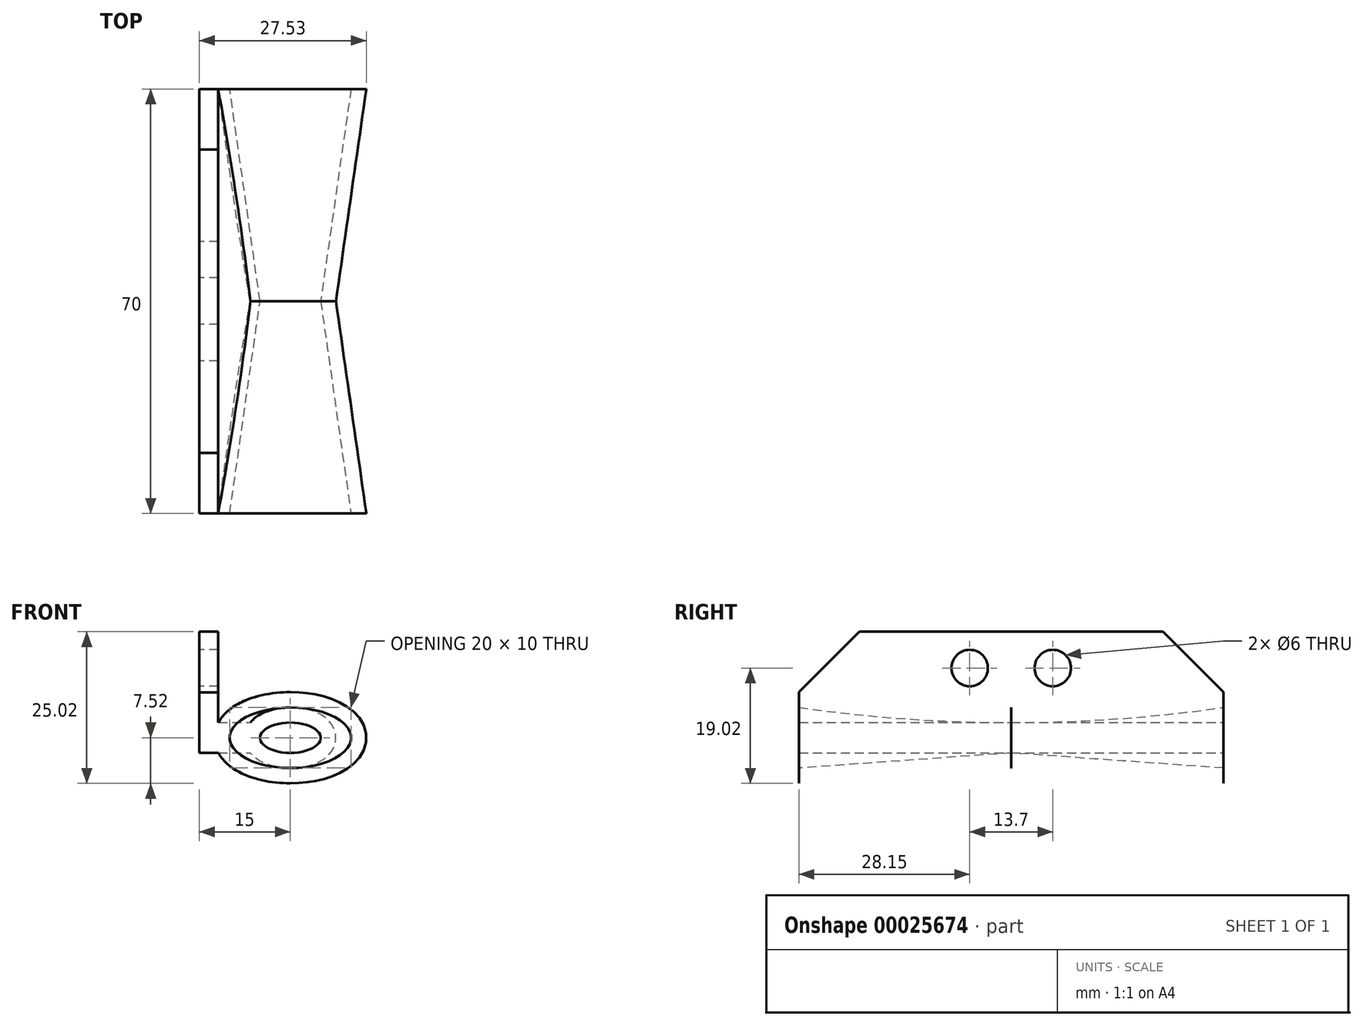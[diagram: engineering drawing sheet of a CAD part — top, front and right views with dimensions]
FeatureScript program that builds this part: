
annotation { "Feature Type Name" : "Feature", "Feature Type Description" : "" }
export const myFeature = defineFeature(function(context is Context, id is Id, definition is map)
    precondition{}
    {
        {
            var Q0;
            Q0=qCreatedBy(makeId("Front.planeOp"),FACE);
            var sketch = newSketch(context, id + "F0", { "sketchPlane" : qUnion([Q0])});
            skEllipticalArc(sketch, "E0", {});
            skLineSegment(sketch, "E1", {"start": v(0, -2.5) * mm, "end": v(0, 2.5) * mm});
            const initialGuessF0  = {"E0": [0, 0, 1, 0, 0.005, 0.0025, 4.71238898038469, 1.5707963267948966]};
            skSetInitialGuess(sketch, initialGuessF0);
            skSolve(sketch);
        }
        {
            var Q0;
            Q0=qCreatedBy(makeId("Front.planeOp"),FACE);
            cPlane(context, id + "F1", {"entities" : qUnion([Q0]), "cplaneType" : CPlaneType.OFFSET, "offset" : 35 * mm, "width" : 150 * mm, "height" : 150 * mm});
        }
        {
            var Q0;
            Q0=qCreatedBy(id+"F1.planeOp",FACE);
            var sketch = newSketch(context, id + "F2", { "sketchPlane" : qUnion([Q0])});
            skEllipticalArc(sketch, "E2", {});
            skLineSegment(sketch, "E3", {"start": v(0, -5) * mm, "end": v(0, 5) * mm});
            const initialGuessF2  = {"E2": [0, 0, 1, 0, 0.01, 0.005, 4.71238898038469, 1.5707963267948966]};
            skSetInitialGuess(sketch, initialGuessF2);
            skSolve(sketch);
        }
        {
            var Q0;
            Q0=qCreatedBy(makeId("Right.planeOp"),FACE);
            var sketch = newSketch(context, id + "F3", { "sketchPlane" : qUnion([Q0])});
            skArc(sketch, "E4", {"start": v(-35, 5) * mm, "mid": v(-17.54, 3.13) * mm, "end": v(0, 2.5) * mm});
            skSolve(sketch);
        }
        {
            var Q0;
            Q0=makeQuery(id+"F0.imprint","IMPRINT",FACE,{"disambiguationData":[TD([[makeQuery(id+"F0.imprint","IMPRINT",EDGE,{"derivedFrom":sQuery(id+"F0.wireOp",EDGE,"E0")}),1.0]])]});
            var Q1;
            Q1=makeQuery(id+"F2.imprint","IMPRINT",FACE,{"disambiguationData":[TD([[makeQuery(id+"F2.imprint","IMPRINT",EDGE,{"derivedFrom":sQuery(id+"F2.wireOp",EDGE,"E2")}),1.0]])]});
            var Q2;
            Q2 = qBodyType(qCreatedBy(id + "F3" ,EDGE), BodyType.WIRE);
            loft(context, id + "F4", {"addGuides" : true, "sheetProfilesArray" : [{ "sheetProfileEntities" : qUnion([Q0]) }, { "sheetProfileEntities" : qUnion([Q1]) }], "guidesArray" : [{ "guideEntities" : qUnion([Q2]), "guideDerivativeType" : LoftGuideDerivativeType.DEFAULT, "guideDerivativeMagnitude" : 1 }]});
        }
        {
            var Q0;
            Q0=makeQuery(id+"F4.opLoft","SWEPT_BODY",BODY,{"disambiguationData":[OSD([makeQuery(id+"F0.imprint","IMPRINT",FACE,{"disambiguationData":[TD([[makeQuery(id+"F0.imprint","IMPRINT",EDGE,{"derivedFrom":sQuery(id+"F0.wireOp",EDGE,"E0")}),1.0]])]}),makeQuery(id+"F2.imprint","IMPRINT",FACE,{"disambiguationData":[TD([[makeQuery(id+"F2.imprint","IMPRINT",EDGE,{"derivedFrom":sQuery(id+"F2.wireOp",EDGE,"E2")}),1.0]])]}),sQuery(id+"F3.wireOp",EDGE,"E4")])]});
            var Q1;
            Q1=qCreatedBy(makeId("Right.planeOp"),FACE);
            mirror(context, id + "F5", {"operationType" : NewBodyOperationType.ADD, "entities" : qUnion([Q0]), "mirrorPlane" : qUnion([Q1])});
        }
        {
            var Q0;
            Q0=makeQuery(id+"F4.opLoft","SWEPT_BODY",BODY,{"disambiguationData":[OSD([makeQuery(id+"F0.imprint","IMPRINT",FACE,{"disambiguationData":[TD([[makeQuery(id+"F0.imprint","IMPRINT",EDGE,{"derivedFrom":sQuery(id+"F0.wireOp",EDGE,"E0")}),1.0]])]}),makeQuery(id+"F2.imprint","IMPRINT",FACE,{"disambiguationData":[TD([[makeQuery(id+"F2.imprint","IMPRINT",EDGE,{"derivedFrom":sQuery(id+"F2.wireOp",EDGE,"E2")}),1.0]])]}),sQuery(id+"F3.wireOp",EDGE,"E4")])]});
            var Q1;
            Q1=qCreatedBy(makeId("Front.planeOp"),FACE);
            mirror(context, id + "F6", {"operationType" : NewBodyOperationType.ADD, "entities" : qUnion([Q0]), "mirrorPlane" : qUnion([Q1])});
        }
        {
            var Q0;
            {var subQ0=makeQuery(id+"F4.opLoft","CAP_FACE",FACE,{"disambiguationData":[OSD([makeQuery(id+"F2.imprint","IMPRINT",FACE,{"disambiguationData":[TD([[makeQuery(id+"F2.imprint","IMPRINT",EDGE,{"derivedFrom":sQuery(id+"F2.wireOp",EDGE,"E2")}),1.0]])]})])],"isStart":true});Q0=makeQuery(id+"F5.boolean.opBoolean","MERGE",FACE,{"derivedFrom":[subQ0,makeQuery(id+"F5.opPattern","COPY",FACE,{"derivedFrom":subQ0,"instanceName":"1"})]});}
            var Q1;
            {var subQ0=makeQuery(id+"F4.opLoft","CAP_FACE",FACE,{"disambiguationData":[OSD([makeQuery(id+"F2.imprint","IMPRINT",FACE,{"disambiguationData":[TD([[makeQuery(id+"F2.imprint","IMPRINT",EDGE,{"derivedFrom":sQuery(id+"F2.wireOp",EDGE,"E2")}),1.0]])]})])],"isStart":true});Q1=makeQuery(id+"F6.opPattern","COPY",FACE,{"derivedFrom":makeQuery(id+"F5.boolean.opBoolean","MERGE",FACE,{"derivedFrom":[subQ0,makeQuery(id+"F5.opPattern","COPY",FACE,{"derivedFrom":subQ0,"instanceName":"1"})]}),"instanceName":"1"});}
            shell(context, id + "F7", {"entities" : qUnion([Q0, Q1]), "thickness" : 2.5 * mm, "oppositeDirection" : true});
        }
        {
            var Q0;
            Q0=qCreatedBy(makeId("Right.planeOp"),FACE);
            cPlane(context, id + "F8", {"entities" : qUnion([Q0]), "cplaneType" : CPlaneType.OFFSET, "offset" : 15 * mm, "oppositeDirection" : true, "width" : 150 * mm, "height" : 150 * mm});
        }
        {
            var Q0;
            Q0=qCreatedBy(id+"F8.planeOp",FACE);
            var sketch = newSketch(context, id + "F9", { "sketchPlane" : qUnion([Q0])});
            skLineSegment(sketch, "E5.bottom", {"start": v(35, -2.5) * mm, "end": v(-35, -2.5) * mm});
            skLineSegment(sketch, "E5.top", {"start": v(35, 2.5) * mm, "end": v(-35, 2.5) * mm});
            skLineSegment(sketch, "E5.left", {"start": v(35, -2.5) * mm, "end": v(35, 2.5) * mm});
            skLineSegment(sketch, "E5.right", {"start": v(-35, -2.5) * mm, "end": v(-35, 2.5) * mm});
            skSolve(sketch);
        }
        {
            var Q0;
            Q0 = qSketchRegion(id + "F9", true);
            extrude(context, id + "F10", {"entities" : qUnion([Q0]), "operationType" : NewBodyOperationType.ADD, "endBound" : BoundingType.UP_TO_NEXT, "depth" : 25 * mm});
        }
        {
            var Q0;
            Q0=makeQuery(id+"F10.opExtrude","SWEPT_FACE",FACE,{"disambiguationData":[OSD([sQuery(id+"F9.wireOp",EDGE,"E5.top")])]});
            var sketch = newSketch(context, id + "F11", { "sketchPlane" : qUnion([Q0])});
            skLineSegment(sketch, "E6.bottom", {"start": v(-15, -35) * mm, "end": v(-11.88, -35) * mm});
            skLineSegment(sketch, "E6.top", {"start": v(-15, 35) * mm, "end": v(-11.88, 35) * mm});
            skLineSegment(sketch, "E6.left", {"start": v(-15, -35) * mm, "end": v(-15, 35) * mm});
            skLineSegment(sketch, "E6.right", {"start": v(-11.88, -35) * mm, "end": v(-11.88, 35) * mm});
            skSolve(sketch);
        }
        {
            var Q0;
            Q0 = qSketchRegion(id + "F11", true);
            extrude(context, id + "F12", {"entities" : qUnion([Q0]), "operationType" : NewBodyOperationType.ADD, "depth" : 15 * mm});
        }
        {
            var Q0;
            Q0=makeQuery(id+"F12.boolean.opBoolean","MERGE",FACE,{"derivedFrom":[makeQuery(id+"F10.opExtrude","CAP_FACE",FACE,{"disambiguationData":[OSD([sQuery(id+"F9.wireOp",EDGE,"E5.bottom"),sQuery(id+"F9.wireOp",EDGE,"E5.top"),sQuery(id+"F9.wireOp",EDGE,"E5.left"),sQuery(id+"F9.wireOp",EDGE,"E5.right")])],"isStart":true}),makeQuery(id+"F12.opExtrude","SWEPT_FACE",FACE,{"disambiguationData":[OSD([sQuery(id+"F11.wireOp",EDGE,"E6.left")])]})]});
            var sketch = newSketch(context, id + "F13", { "sketchPlane" : qUnion([Q0])});
            skPoint(sketch, "E7", {"position": v(6.85, 11.5) * mm});
            skLineSegment(sketch, "E8", {"start": v(0, 0) * mm, "end": v(0, 17.5) * mm, "construction": true});
            skPoint(sketch, "E9.MirrorP", {"position": v(-6.85, 11.5) * mm});
            skSolve(sketch);
        }
        {
            var Q0;
            Q0=sQuery(id+"F13.wireOp",VERTEX,"E7");
            var Q1;
            Q1=sQuery(id+"F13.wireOp",VERTEX,"E9.MirrorP");
            var Q2;
            Q2=makeQuery(id+"F4.opLoft","SWEPT_BODY",BODY,{"disambiguationData":[OSD([makeQuery(id+"F0.imprint","IMPRINT",FACE,{"disambiguationData":[TD([[makeQuery(id+"F0.imprint","IMPRINT",EDGE,{"derivedFrom":sQuery(id+"F0.wireOp",EDGE,"E0")}),1.0]])]}),makeQuery(id+"F2.imprint","IMPRINT",FACE,{"disambiguationData":[TD([[makeQuery(id+"F2.imprint","IMPRINT",EDGE,{"derivedFrom":sQuery(id+"F2.wireOp",EDGE,"E2")}),1.0]])]}),sQuery(id+"F3.wireOp",EDGE,"E4")])]});
            hole(context, id + "F14", {"style" : HoleStyle.SIMPLE, "holeDiameter" : 6 * mm, "endStyle" : HoleEndStyle.THROUGH, "locations" : qUnion([Q0, Q1]), "scope" : qUnion([Q2])});
        }
        {
            var Q0;
            Q0=makeQuery(id+"F12.opExtrude","CAP_EDGE",EDGE,{"disambiguationData":[OSD([sQuery(id+"F11.wireOp",EDGE,"E6.bottom")])],"isStart":false});
            var Q1;
            Q1=makeQuery(id+"F12.opExtrude","CAP_EDGE",EDGE,{"disambiguationData":[OSD([sQuery(id+"F11.wireOp",EDGE,"E6.top")])],"isStart":false});
            chamfer(context, id + "F15", {"entities" : qUnion([Q0, Q1]), "width" : 10 * mm, "tangentPropagation" : true});
        }
    });
